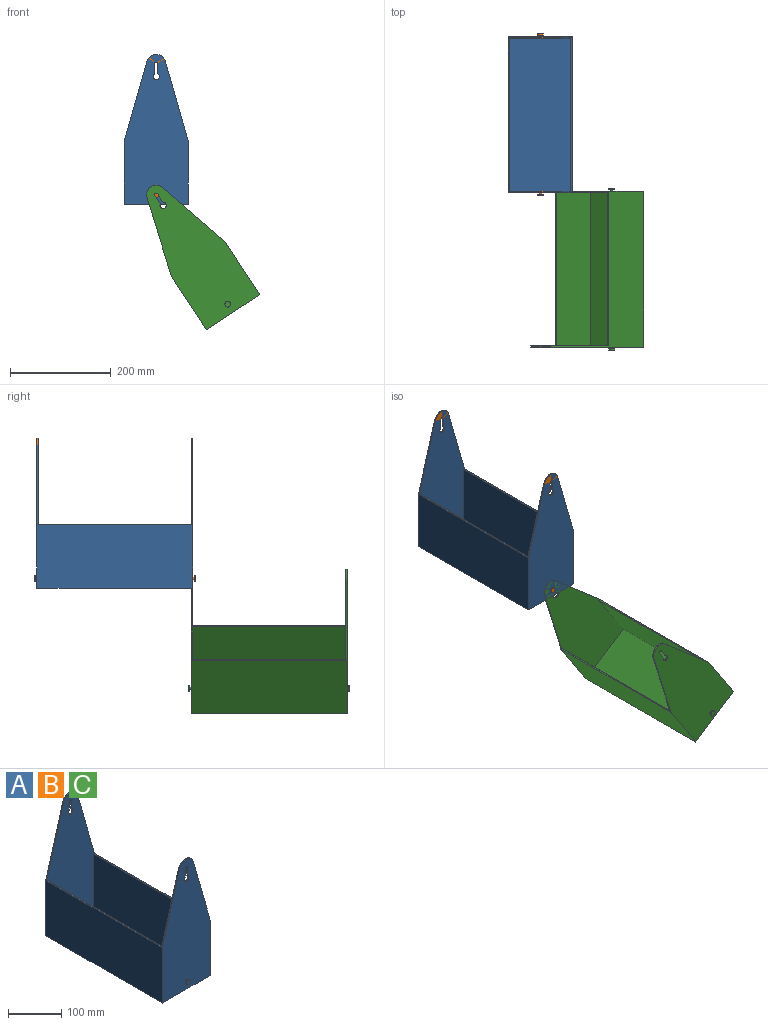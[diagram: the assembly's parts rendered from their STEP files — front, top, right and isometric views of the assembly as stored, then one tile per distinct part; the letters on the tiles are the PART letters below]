
ASSEMBLY  parts=3 mates=1
PART A: 36 faces, bbox 127x321.3x298.5 mm
  f0: plane 304.8x2.64mm, normal (0,0,1), area 805.4mm2, adj f1,f5,f21,f27
  f1: plane 295.91x127mm, normal (0,1,0), area 28179.2mm2, adj f0,f2,f3,f4,f7,f8,f9,f10
  f2: plane 157.65x45.19mm, normal (0.96,0,0.28), area 416.6mm2, adj f1,f3,f11,f12
  f3: cylinder r=19.05mm len=36.63mm, axis (0,1,0), area 125mm2, adj f1,f2,f4,f12
  f4: plane 157.65x45.19mm, normal (-0.96,0,0.28), area 416.6mm2, adj f1,f3,f5,f12
  f5: plane 309.88x127mm, normal (-1,0,0), area 39354.8mm2, adj f0,f4,f6,f12,f15,f20
  f6: plane 309.88x127mm, normal (0,0,-1), area 39354.8mm2, adj f5,f11,f12,f20
  f7: cylinder r=6.35mm len=12.7mm, axis (0,1,0), area 84.5mm2, adj f1,f8,f10,f12
  f8: plane 19.9x2.54mm, normal (1,0,0), area 50.5mm2, adj f1,f7,f9,f12
  f9: cylinder r=3.17mm len=6.35mm, axis (0,1,0), area 25.3mm2, adj f1,f8,f10,f12
  f10: plane 19.9x2.54mm, normal (-1,0,0), area 50.5mm2, adj f1,f7,f9,f12
  f11: plane 309.88x127mm, normal (1,0,0), area 39354.8mm2, adj f2,f6,f12,f13,f20,f22
  f12: plane 298.45x127mm, normal (0,-1,0), area 29102.4mm2, adj f2,f3,f4,f5,f6,f7,f8,f9
  f13: plane 157.65x45.19mm, normal (0.96,0,0.28), area 416.6mm2, adj f11,f14,f20,f21
  f14: cylinder r=19.05mm len=36.63mm, axis (0,-1,0), area 125mm2, adj f13,f15,f20,f21
  f15: plane 157.65x45.19mm, normal (-0.96,0,0.28), area 416.6mm2, adj f5,f14,f20,f21
  f16: cylinder r=6.35mm len=12.7mm, axis (0,-1,0), area 84.5mm2, adj f17,f19,f20,f21
  f17: plane 19.9x2.54mm, normal (1,0,0), area 50.5mm2, adj f16,f18,f20,f21
  f18: cylinder r=3.17mm len=6.35mm, axis (0,-1,0), area 25.3mm2, adj f17,f19,f20,f21
  f19: plane 19.9x2.54mm, normal (-1,0,0), area 50.5mm2, adj f16,f18,f20,f21
  f20: plane 298.45x127mm, normal (0,1,0), area 29102.4mm2, adj f5,f6,f11,f13,f14,f15,f16,f17
  f21: plane 295.91x127mm, normal (0,-1,0), area 28179.2mm2, adj f0,f13,f14,f15,f16,f17,f18,f19
  f22: plane 304.8x2.64mm, normal (0,0,1), area 805.4mm2, adj f1,f11,f21,f26
  f23: plane 304.8x124.1mm, normal (1,0,0), area 37826.6mm2, adj f1,f21,f24,f27
  f24: plane 304.8x121.92mm, normal (0,0,1), area 37161.2mm2, adj f1,f21,f23,f25
  f25: plane 304.8x124.1mm, normal (-1,0,0), area 37826.6mm2, adj f1,f21,f24,f26
  f26: plane 304.8x0.36mm, normal (-0.96,0,-0.28), area 113.1mm2, adj f1,f21,f22,f25
  f27: plane 304.8x0.36mm, normal (0.96,0,-0.28), area 113.1mm2, adj f0,f1,f21,f23
  f28: cylinder r=3.17mm len=6.35mm, axis (0,1,0), area 63.3mm2, adj f12,f31
  f29: cylinder r=5.71mm len=11.43mm, axis (0,1,0), area 91.2mm2, adj f30,f31
  f30: plane 11.43x11.43mm, normal (0,-1,0), area 102.6mm2, adj f29
  f31: plane 11.43x11.43mm, normal (0,1,0), area 70.9mm2, adj f28,f29
  f32: cylinder r=3.17mm len=6.35mm, axis (0,-1,0), area 63.3mm2, adj f20,f35
  f33: cylinder r=5.71mm len=11.43mm, axis (0,-1,0), area 91.2mm2, adj f34,f35
  f34: plane 11.43x11.43mm, normal (0,1,0), area 102.6mm2, adj f33
  f35: plane 11.43x11.43mm, normal (0,-1,0), area 70.9mm2, adj f32,f33
PART B: same geometry as A
PART C: same geometry as A
PLACE A t=(-129.32,-130.28,59.46)mm
PLACE B t=(-129.32,-130.28,59.46)mm fixed
PLACE C rot(axis=(0.29,0,-0.96),180deg) t=(-11.24,-132.82,-165.74)mm
MATE revolute B.f28 <-> C.f3  axis (0,1,0) through (-129.32,-132.82,15.01)mm
